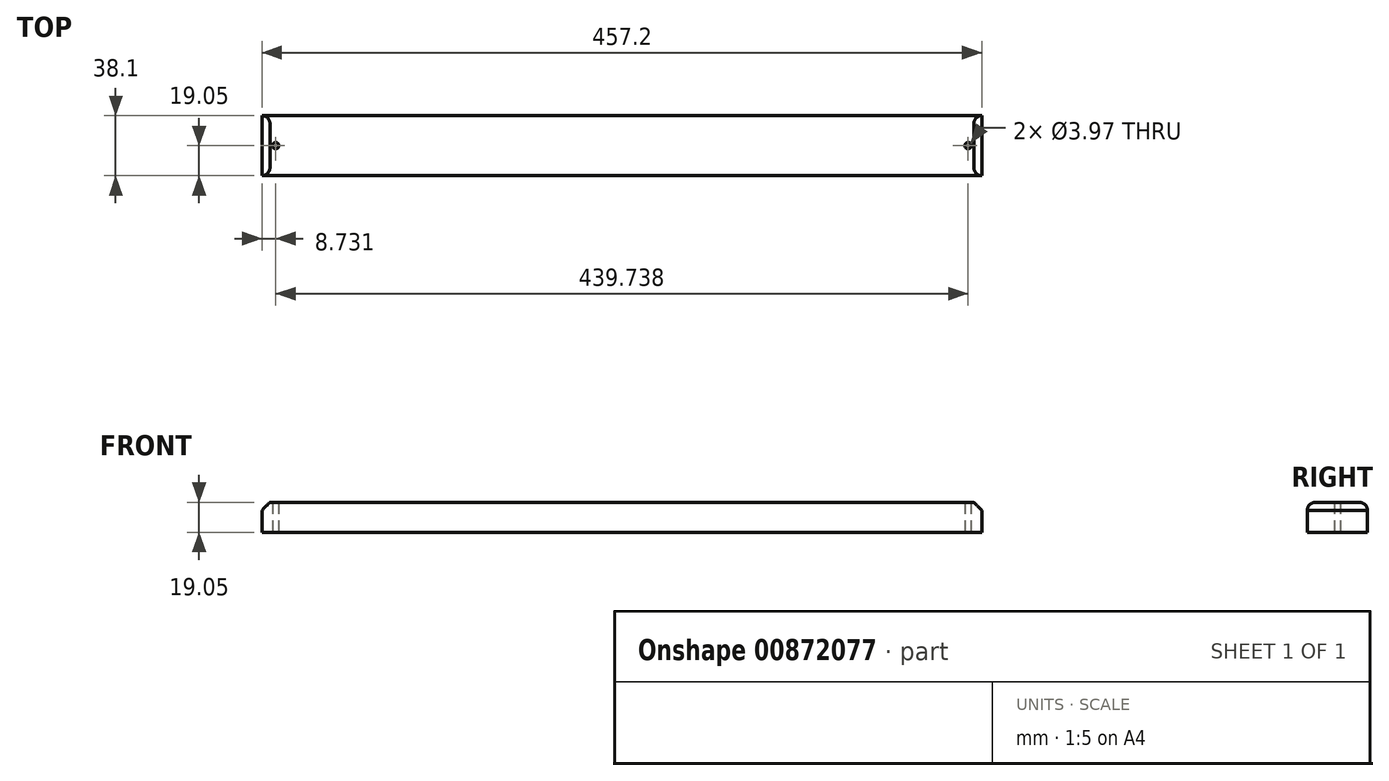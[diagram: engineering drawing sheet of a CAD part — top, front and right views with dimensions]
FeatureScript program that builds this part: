
annotation { "Feature Type Name" : "Feature", "Feature Type Description" : "" }
export const myFeature = defineFeature(function(context is Context, id is Id, definition is map)
    precondition{}
    {
        {
            var Q0;
            Q0=qCreatedBy(makeId("Top.planeOp"),FACE);
            var sketch = newSketch(context, id + "F0", { "sketchPlane" : qUnion([Q0])});
            skLineSegment(sketch, "E0.bottom", {"start": v(0, 0) * mm, "end": v(457.2, 0) * mm});
            skLineSegment(sketch, "E0.top", {"start": v(0, 38.1) * mm, "end": v(457.2, 38.1) * mm});
            skLineSegment(sketch, "E0.left", {"start": v(0, 0) * mm, "end": v(0, 38.1) * mm});
            skLineSegment(sketch, "E0.right", {"start": v(457.2, 0) * mm, "end": v(457.2, 38.1) * mm});
            skCircle(sketch, "E1", {"center": v(8.73, 19.05) * mm, "radius": 1.98 * mm});
            skLineSegment(sketch, "E2", {"start": v(228.6, 55.2) * mm, "end": v(228.6, -40.25) * mm, "construction": true});
            skPoint(sketch, "E2.startSnap0", {"position": v(228.6, 38.1) * mm});
            skCircle(sketch, "E3.MirrorC", {"center": v(448.47, 19.05) * mm, "radius": 1.98 * mm});
            skLineSegment(sketch, "E4", {"start": v(17.46, 45.5) * mm, "end": v(17.46, -18) * mm, "construction": true});
            skSolve(sketch);
        }
        {
            var Q0;
            Q0=qSketchRegion(id+"F0",true);
            extrude(context, id + "F1", {"entities" : qUnion([Q0]), "depth" : 19.05 * mm});
        }
        {
            var Q0;
            Q0=makeQuery(id+"F1.opExtrude","CAP_EDGE",EDGE,{"disambiguationData":[OSD([sQuery(id+"F0.wireOp",EDGE,"E0.left")])],"isStart":false});
            var Q1;
            Q1=makeQuery(id+"F1.opExtrude","CAP_EDGE",EDGE,{"disambiguationData":[OSD([sQuery(id+"F0.wireOp",EDGE,"E0.right")])],"isStart":false});
            chamfer(context, id + "F2", {"entities" : qUnion([Q0, Q1]), "width" : 5.08 * mm, "tangentPropagation" : true});
        }
        {
            var Q0;
            Q0=makeQuery(id+"F1.opExtrude","CAP_EDGE",EDGE,{"disambiguationData":[OSD([sQuery(id+"F0.wireOp",EDGE,"E0.top")])],"isStart":false});
            var Q1;
            Q1=makeQuery(id+"F1.opExtrude","CAP_EDGE",EDGE,{"disambiguationData":[OSD([sQuery(id+"F0.wireOp",EDGE,"E0.bottom")])],"isStart":false});
            fillet(context, id + "F3", {"entities" : qUnion([Q0, Q1]), "radius" : 5.08 * mm, "tangentPropagation" : true, "allowEdgeOverflow" : false});
        }
    });
